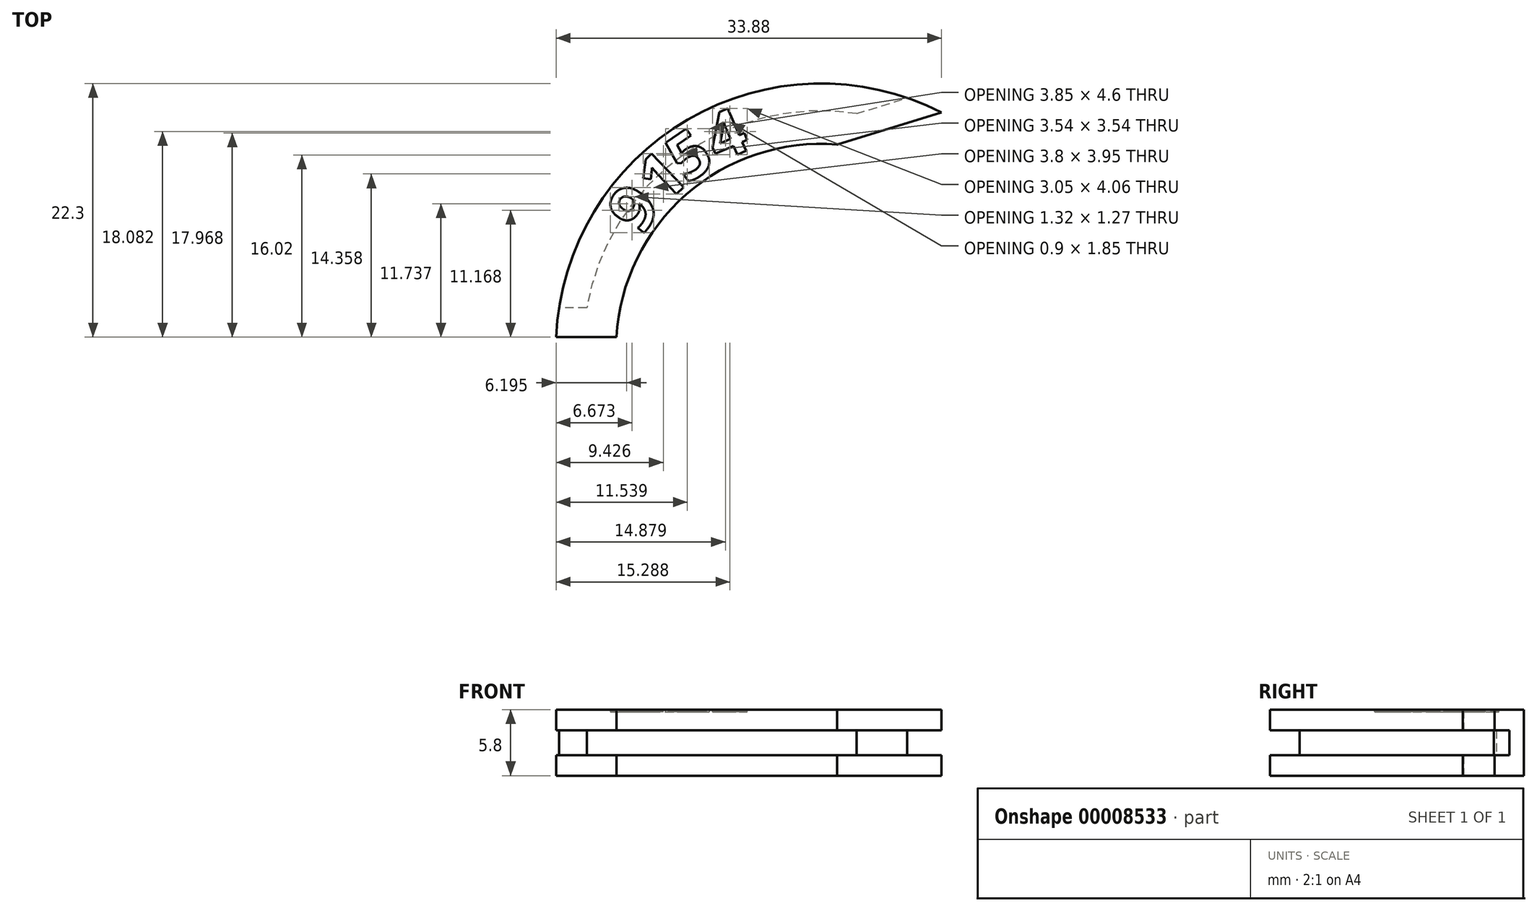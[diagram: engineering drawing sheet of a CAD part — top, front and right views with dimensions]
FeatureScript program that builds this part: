
annotation { "Feature Type Name" : "Feature", "Feature Type Description" : "" }
export const myFeature = defineFeature(function(context is Context, id is Id, definition is map)
    precondition{}
    {
        {
            var Q0;
            Q0=qCreatedBy(makeId("Top.planeOp"),FACE);
            var sketch = newSketch(context, id + "F0", { "sketchPlane" : qUnion([Q0])});
            skArc(sketch, "E0", {"start": v(1.42, 17.94) * mm, "mid": v(-11.84, 13.56) * mm, "end": v(-17.97, 1) * mm});
            skArc(sketch, "E1", {"start": v(10.6, 20.75) * mm, "mid": v(-11.73, 20.13) * mm, "end": v(-23.28, 1) * mm});
            skArc(sketch, "E2", {"start": v(7.07, 19.67) * mm, "mid": v(-11.61, 17.38) * mm, "end": v(-20.88, 1) * mm});
            skLineSegment(sketch, "E3", {"start": v(0, 0) * mm, "end": v(-18, 0) * mm});
            skLineSegment(sketch, "E4", {"start": v(-54, 0) * mm, "end": v(32.96, 26.59) * mm});
            skLineSegment(sketch, "E5.0", {"start": v(0, 1) * mm, "end": v(-54, 1) * mm});
            skLineSegment(sketch, "E6", {"start": v(-54, 1) * mm, "end": v(-11.21, 14.08) * mm});
            skLineSegment(sketch, "E7.trimOffspring", {"start": v(-23.3, 0) * mm, "end": v(-54, 0) * mm});
            skLineSegment(sketch, "E8.trimOffspring", {"start": v(1.42, 17.94) * mm, "end": v(32.65, 27.5) * mm});
            skSolve(sketch);
        }
        {
            var Q0;
            {var subQ0=sQuery(id+"F0.wireOp",EDGE,"E8.trimOffspring");var subQ1=sQuery(id+"F0.wireOp",EDGE,"E0");var subQ2=makeQuery(id+"F0.imprint","INTERSECT",VERTEX,{"derivedFrom":[subQ1,subQ0]});Q0=makeQuery(id+"F0.imprint","IMPRINT",FACE,{"disambiguationData":[TD([[makeQuery(id+"F0.imprint","IMPRINT",EDGE,{"disambiguationData":[TD([[subQ2,-1.0]])],"derivedFrom":subQ1}),-1.0]])]});}
            var Q1;
            {var subQ0=sQuery(id+"F0.wireOp",EDGE,"E5.0");var subQ1=sQuery(id+"F0.wireOp",EDGE,"E0");var subQ2=makeQuery(id+"F0.imprint","INTERSECT",VERTEX,{"derivedFrom":[subQ1,subQ0]});Q1=makeQuery(id+"F0.imprint","IMPRINT",FACE,{"disambiguationData":[TD([[makeQuery(id+"F0.imprint","IMPRINT",EDGE,{"disambiguationData":[TD([[subQ2,1.0]])],"derivedFrom":subQ1}),-1.0]])]});}
            var Q2;
            {var subQ0=sQuery(id+"F0.wireOp",EDGE,"E8.trimOffspring");var subQ1=sQuery(id+"F0.wireOp",EDGE,"E1");var subQ2=makeQuery(id+"F0.imprint","INTERSECT",VERTEX,{"derivedFrom":[subQ1,subQ0]});Q2=makeQuery(id+"F0.imprint","IMPRINT",FACE,{"disambiguationData":[TD([[makeQuery(id+"F0.imprint","IMPRINT",EDGE,{"disambiguationData":[TD([[subQ2,-1.0]])],"derivedFrom":subQ1}),1.0]])]});}
            var Q3;
            {var subQ0=sQuery(id+"F0.wireOp",EDGE,"E6");var subQ1=sQuery(id+"F0.wireOp",EDGE,"E0");var subQ2=makeQuery(id+"F0.imprint","INTERSECT",VERTEX,{"derivedFrom":[subQ1,subQ0]});Q3=makeQuery(id+"F0.imprint","IMPRINT",FACE,{"disambiguationData":[TD([[makeQuery(id+"F0.imprint","IMPRINT",EDGE,{"disambiguationData":[TD([[subQ2,-1.0]])],"derivedFrom":subQ1}),-1.0]])]});}
            var Q4;
            {var subQ0=sQuery(id+"F0.wireOp",EDGE,"E5.0");var subQ1=sQuery(id+"F0.wireOp",EDGE,"E1");var subQ2=makeQuery(id+"F0.imprint","INTERSECT",VERTEX,{"derivedFrom":[subQ1,subQ0]});Q4=makeQuery(id+"F0.imprint","IMPRINT",FACE,{"disambiguationData":[TD([[makeQuery(id+"F0.imprint","IMPRINT",EDGE,{"disambiguationData":[TD([[subQ2,1.0]])],"derivedFrom":subQ1}),1.0]])]});}
            var Q5;
            {var subQ0=sQuery(id+"F0.wireOp",EDGE,"E6");var subQ1=sQuery(id+"F0.wireOp",EDGE,"E1");var subQ2=makeQuery(id+"F0.imprint","INTERSECT",VERTEX,{"derivedFrom":[subQ1,subQ0]});Q5=makeQuery(id+"F0.imprint","IMPRINT",FACE,{"disambiguationData":[TD([[makeQuery(id+"F0.imprint","IMPRINT",EDGE,{"disambiguationData":[TD([[subQ2,-1.0]])],"derivedFrom":subQ1}),1.0]])]});}
            extrude(context, id + "F1", {"entities" : qUnion([Q0, Q1, Q2, Q3, Q4, Q5]), "depth" : 5.8 * mm, "offsetDistance" : 25 * mm});
        }
        {
            var Q0;
            {var subQ0=sQuery(id+"F0.wireOp",EDGE,"E5.0");var subQ1=sQuery(id+"F0.wireOp",EDGE,"E0");var subQ2=makeQuery(id+"F0.imprint","INTERSECT",VERTEX,{"derivedFrom":[subQ1,subQ0]});Q0=makeQuery(id+"F0.imprint","IMPRINT",FACE,{"disambiguationData":[TD([[makeQuery(id+"F0.imprint","IMPRINT",EDGE,{"disambiguationData":[TD([[subQ2,1.0]])],"derivedFrom":subQ1}),-1.0]])]});}
            var Q1;
            {var subQ0=sQuery(id+"F0.wireOp",EDGE,"E6");var subQ1=sQuery(id+"F0.wireOp",EDGE,"E0");var subQ2=makeQuery(id+"F0.imprint","INTERSECT",VERTEX,{"derivedFrom":[subQ1,subQ0]});Q1=makeQuery(id+"F0.imprint","IMPRINT",FACE,{"disambiguationData":[TD([[makeQuery(id+"F0.imprint","IMPRINT",EDGE,{"disambiguationData":[TD([[subQ2,-1.0]])],"derivedFrom":subQ1}),-1.0]])]});}
            var Q2;
            {var subQ0=sQuery(id+"F0.wireOp",EDGE,"E8.trimOffspring");var subQ1=sQuery(id+"F0.wireOp",EDGE,"E0");var subQ2=makeQuery(id+"F0.imprint","INTERSECT",VERTEX,{"derivedFrom":[subQ1,subQ0]});Q2=makeQuery(id+"F0.imprint","IMPRINT",FACE,{"disambiguationData":[TD([[makeQuery(id+"F0.imprint","IMPRINT",EDGE,{"disambiguationData":[TD([[subQ2,-1.0]])],"derivedFrom":subQ1}),-1.0]])]});}
            extrude(context, id + "F2", {"entities" : qUnion([Q0, Q1, Q2]), "operationType" : NewBodyOperationType.REMOVE, "depth" : 4 * mm, "offsetDistance" : 25 * mm, "hasSecondDirection" : true, "secondDirectionOppositeDirection" : false, "secondDirectionDepth" : 1.8 * mm});
        }
        {
            var Q0;
            Q0=makeQuery(id+"F1.opExtrude","SWEPT_FACE",FACE,{"disambiguationData":[OSD([sQuery(id+"F0.wireOp",EDGE,"E5.0")])]});
            var sketch = newSketch(context, id + "F3", { "sketchPlane" : qUnion([Q0])});
            skLineSegment(sketch, "E9.0.0", {"start": v(-17.97, 0) * mm, "end": v(-17.97, 1.8) * mm});
            skLineSegment(sketch, "E9.0.1", {"start": v(-17.97, 1.8) * mm, "end": v(-20.88, 1.8) * mm});
            skLineSegment(sketch, "E9.0.2", {"start": v(-20.88, 1.8) * mm, "end": v(-20.88, 4) * mm});
            skLineSegment(sketch, "E9.0.3", {"start": v(-20.88, 4) * mm, "end": v(-17.97, 4) * mm});
            skLineSegment(sketch, "E9.0.4", {"start": v(-17.97, 4) * mm, "end": v(-17.97, 5.8) * mm});
            skLineSegment(sketch, "E9.0.5", {"start": v(-17.97, 5.8) * mm, "end": v(-23.28, 5.8) * mm});
            skLineSegment(sketch, "E9.0.6", {"start": v(-23.28, 5.8) * mm, "end": v(-23.28, 0) * mm});
            skLineSegment(sketch, "E9.0.7", {"start": v(-23.28, 0) * mm, "end": v(-17.97, 0) * mm});
            skLineSegment(sketch, "E10", {"start": v(-20.88, 4) * mm, "end": v(-23.28, 4) * mm});
            skLineSegment(sketch, "E11", {"start": v(-20.88, 1.8) * mm, "end": v(-23.28, 1.8) * mm});
            skPoint(sketch, "E11.endSnap0", {"position": v(-23.28, 2.9) * mm});
            skLineSegment(sketch, "E12", {"start": v(-17.97, 4) * mm, "end": v(-17.97, 1.8) * mm});
            skSolve(sketch);
        }
        {
            var Q0;
            Q0=makeQuery(id+"F3.imprint","IMPRINT",FACE,{"disambiguationData":[TD([[makeQuery(id+"F3.imprint","IMPRINT",EDGE,{"derivedFrom":sQuery(id+"F3.wireOp",EDGE,"E9.0.1")}),-1.0]])]});
            var Q1;
            Q1=makeQuery(id+"F3.imprint","IMPRINT",FACE,{"disambiguationData":[TD([[makeQuery(id+"F3.imprint","IMPRINT",EDGE,{"derivedFrom":sQuery(id+"F3.wireOp",EDGE,"E9.0.2")}),-1.0]])]});
            extrude(context, id + "F4", {"entities" : qUnion([Q0, Q1]), "operationType" : NewBodyOperationType.REMOVE, "oppositeDirection" : true, "depth" : 2.6 * mm, "offsetDistance" : 25 * mm});
        }
        {
            var Q0;
            Q0=makeQuery(id+"F1.opExtrude","SWEPT_FACE",FACE,{"disambiguationData":[OSD([sQuery(id+"F0.wireOp",EDGE,"E8.trimOffspring")])]});
            var sketch = newSketch(context, id + "F5", { "sketchPlane" : qUnion([Q0])});
            skLineSegment(sketch, "E13.0.0", {"start": v(12.5, 1.8) * mm, "end": v(6.6, 1.8) * mm});
            skLineSegment(sketch, "E13.0.1", {"start": v(6.6, 1.8) * mm, "end": v(6.6, 0) * mm});
            skLineSegment(sketch, "E13.0.2", {"start": v(6.6, 0) * mm, "end": v(16.2, 0) * mm});
            skLineSegment(sketch, "E13.0.3", {"start": v(16.2, 0) * mm, "end": v(16.2, 5.8) * mm});
            skLineSegment(sketch, "E13.0.4", {"start": v(16.2, 5.8) * mm, "end": v(6.6, 5.8) * mm});
            skLineSegment(sketch, "E13.0.5", {"start": v(6.6, 5.8) * mm, "end": v(6.6, 4) * mm});
            skLineSegment(sketch, "E13.0.6", {"start": v(6.6, 4) * mm, "end": v(12.5, 4) * mm});
            skLineSegment(sketch, "E13.0.7", {"start": v(12.5, 4) * mm, "end": v(12.5, 1.8) * mm});
            skLineSegment(sketch, "E14", {"start": v(6.6, 4) * mm, "end": v(6.6, 1.8) * mm});
            skLineSegment(sketch, "E15", {"start": v(12.5, 4) * mm, "end": v(16.2, 4) * mm});
            skLineSegment(sketch, "E16", {"start": v(12.5, 1.8) * mm, "end": v(16.2, 1.8) * mm});
            skSolve(sketch);
        }
        {
            var Q0;
            Q0=makeQuery(id+"F5.imprint","IMPRINT",FACE,{"disambiguationData":[TD([[makeQuery(id+"F5.imprint","IMPRINT",EDGE,{"derivedFrom":sQuery(id+"F5.wireOp",EDGE,"E13.0.0")}),1.0]])]});
            var Q1;
            Q1=makeQuery(id+"F5.imprint","IMPRINT",FACE,{"disambiguationData":[TD([[makeQuery(id+"F5.imprint","IMPRINT",EDGE,{"derivedFrom":sQuery(id+"F5.wireOp",EDGE,"E13.0.7")}),1.0]])]});
            extrude(context, id + "F6", {"entities" : qUnion([Q0, Q1]), "operationType" : NewBodyOperationType.REMOVE, "oppositeDirection" : true, "depth" : 2.1 * mm, "offsetDistance" : 25 * mm});
        }
        {
            var Q0;
            Q0=makeQuery(id+"F1.opExtrude","CAP_FACE",FACE,{"disambiguationData":[OSD([sQuery(id+"F0.wireOp",EDGE,"E0"),sQuery(id+"F0.wireOp",EDGE,"E1"),sQuery(id+"F0.wireOp",EDGE,"E5.0"),sQuery(id+"F0.wireOp",EDGE,"E8.trimOffspring")])],"isStart":false});
            var sketch = newSketch(context, id + "F7", { "sketchPlane" : qUnion([Q0])});
            skText(sketch, "E17", { "text": "9", "fontName": "NotoSans-Bold.ttf"});
            skCircle(sketch, "E18", {"center": v(0, 0) * mm, "radius": 18.65 * mm});
            skText(sketch, "E19", { "text": "1", "fontName": "OpenSans-Bold.ttf"});
            skText(sketch, "E20", { "text": "5", "fontName": "OpenSans-Bold.ttf"});
            skText(sketch, "E21", { "text": "4", "fontName": "OpenSans-Bold.ttf"});
            const initialGuessF7  = {"E17": [-0.01585, 0.00983, 0.60276, 0.79792, 0.0041], "E19": [-0.01379, 0.01256, 0.72557, 0.68815, 0.0041], "E20": [-0.01181, 0.01443, 0.82782, 0.561, 0.0041], "E21": [-0.00903, 0.01632, 0.91693, 0.39904, 0.0041]};
            skSetInitialGuess(sketch, initialGuessF7);
            skSolve(sketch);
        }
        {
            var Q0;
            {var subQ0=sQuery(id+"F7.wireOp",EDGE,"E17.sketch_text.stroke-2");Q0=makeQuery(id+"F7.imprint","IMPRINT",FACE,{"disambiguationData":[TD([[makeQuery(id+"F7.imprint","IMPRINT",EDGE,{"derivedFrom":subQ0}),-1.0]])]});}
            var Q1;
            {var subQ5=sQuery(id+"F7.wireOp",EDGE,"E21.sketch_text.stroke-2");Q1=makeQuery(id+"F7.imprint","IMPRINT",FACE,{"disambiguationData":[TD([[makeQuery(id+"F7.imprint","IMPRINT",EDGE,{"derivedFrom":subQ5}),-1.0]])]});}
            var Q2;
            Q2=makeQuery(id+"F7.imprint","IMPRINT",FACE,{"disambiguationData":[TD([[makeQuery(id+"F7.imprint","IMPRINT",EDGE,{"derivedFrom":sQuery(id+"F7.wireOp",EDGE,"E20.sketch_text.stroke-0")}),-1.0]])]});
            var Q3;
            {var subQ0=sQuery(id+"F7.wireOp",EDGE,"E20.sketch_text.stroke-3");var subQ1=sQuery(id+"F7.wireOp",EDGE,"E18");var subQ2=makeQuery(id+"F7.imprint","INTERSECT",VERTEX,{"derivedFrom":[subQ1,subQ0]});Q3=makeQuery(id+"F7.imprint","IMPRINT",FACE,{"disambiguationData":[TD([[makeQuery(id+"F7.imprint","IMPRINT",EDGE,{"disambiguationData":[TD([[subQ2,-1.0]])],"derivedFrom":subQ1}),1.0]])]});}
            var Q4;
            {var subQ5=sQuery(id+"F7.wireOp",EDGE,"E19.sketch_text.stroke-0");Q4=makeQuery(id+"F7.imprint","IMPRINT",FACE,{"disambiguationData":[TD([[makeQuery(id+"F7.imprint","IMPRINT",EDGE,{"derivedFrom":subQ5}),-1.0]])]});}
            var Q5;
            {var subQ0=sQuery(id+"F7.wireOp",EDGE,"E19.sketch_text.stroke-2");Q5=makeQuery(id+"F7.imprint","IMPRINT",FACE,{"disambiguationData":[TD([[makeQuery(id+"F7.imprint","IMPRINT",EDGE,{"derivedFrom":subQ0}),-1.0]])]});}
            var Q6;
            {var subQ2=sQuery(id+"F7.wireOp",EDGE,"E17.sketch_text.stroke-0");Q6=makeQuery(id+"F7.imprint","IMPRINT",FACE,{"disambiguationData":[TD([[makeQuery(id+"F7.imprint","IMPRINT",EDGE,{"derivedFrom":subQ2}),-1.0]])]});}
            var Q7;
            {var subQ1=sQuery(id+"F7.wireOp",EDGE,"E21.sketch_text.stroke-0");Q7=makeQuery(id+"F7.imprint","IMPRINT",FACE,{"disambiguationData":[TD([[makeQuery(id+"F7.imprint","IMPRINT",EDGE,{"derivedFrom":subQ1}),-1.0]])]});}
            extrude(context, id + "F8", {"entities" : qUnion([Q0, Q1, Q2, Q3, Q4, Q5, Q6, Q7]), "operationType" : NewBodyOperationType.REMOVE, "oppositeDirection" : true, "depth" : .2 * mm, "offsetDistance" : 25 * mm});
        }
    });
